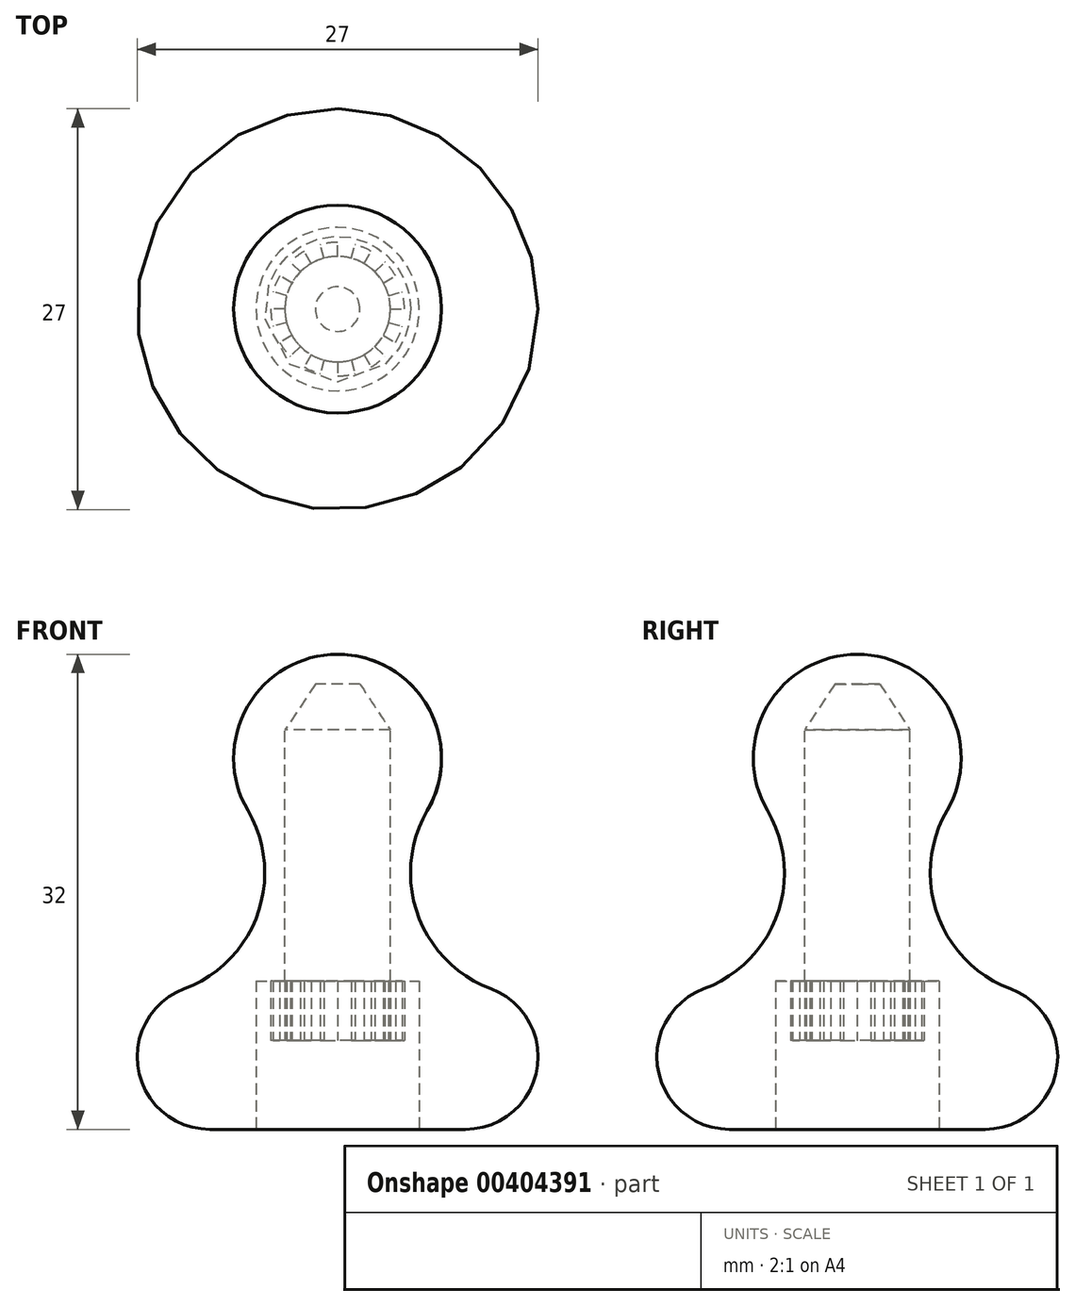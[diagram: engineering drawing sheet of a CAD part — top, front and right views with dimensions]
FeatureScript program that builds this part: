
annotation { "Feature Type Name" : "Feature", "Feature Type Description" : "" }
export const myFeature = defineFeature(function(context is Context, id is Id, definition is map)
    precondition{}
    {
        {
            var Q0;
            Q0=qCreatedBy(makeId("Top.planeOp"),FACE);
            var sketch = newSketch(context, id + "F0", { "sketchPlane" : qUnion([Q0])});
            skCircle(sketch, "E0", {"center": v(0, 0) * mm, "radius": 1.5 * mm});
            skCircle(sketch, "E1", {"center": v(0, 0) * mm, "radius": 3.55 * mm});
            skSolve(sketch);
        }
        {
            var Q0;
            Q0=makeQuery(id+"F0.imprint","IMPRINT",FACE,{"disambiguationData":[TD([[makeQuery(id+"F0.imprint","IMPRINT",EDGE,{"derivedFrom":sQuery(id+"F0.wireOp",EDGE,"BnrdN14r-d7P1-VGVA-sCLp-GcmtuHxksNj9")}),-1.0]])]});
            var Q1;
            Q1=makeQuery(id+"F0.imprint","IMPRINT",FACE,{"disambiguationData":[TD([[makeQuery(id+"F0.imprint","IMPRINT",EDGE,{"derivedFrom":sQuery(id+"F0.wireOp",EDGE,"E0")}),-1.0]])]});
            var Q2;
            Q2=makeQuery(id+"F0.imprint","IMPRINT",FACE,{"disambiguationData":[TD([[makeQuery(id+"F0.imprint","IMPRINT",EDGE,{"derivedFrom":sQuery(id+"F0.wireOp",EDGE,"E0")}),1.0]])]});
            extrude(context, id + "F1", {"entities" : qUnion([Q0, Q1, Q2]), "oppositeDirection" : true, "depth" : 50 * mm});
        }
        {
            var Q0;
            Q0=makeQuery(id+"F1.opExtrude","SWEPT_BODY",BODY,{"disambiguationData":[OSD([sQuery(id+"F0.wireOp",EDGE,"E1")])]});
            var Q1;
            Q1=qCreatedBy(makeId("Origin.pointOp"),VERTEX);
            transform(context, id + "F2", {"entities" : qUnion([Q0]), "transformType" : TransformType.TRANSLATION_3D, "dx" : 0 * mm, "dy" : 0 * mm, "dz" : -3.1 * mm, "makeCopy" : false});
        }
        {
            var Q1;
            Q1=makeQuery(id+"F1.opExtrude","CAP_FACE",FACE,{"disambiguationData":[OSD([sQuery(id+"F0.wireOp",EDGE,"E1")])],"isStart":true});
            var Q2;
            Q2=makeQuery(id+"F0.imprint","IMPRINT",FACE,{"disambiguationData":[TD([[makeQuery(id+"F0.imprint","IMPRINT",EDGE,{"derivedFrom":sQuery(id+"F0.wireOp",EDGE,"E0")}),1.0]])]});
            loft(context, id + "F3", {"operationType" : NewBodyOperationType.ADD, "sheetProfilesArray" : [{ "sheetProfileEntities" : qUnion([Q1]) }, { "sheetProfileEntities" : qUnion([Q2]) }]});
        }
        {
            var Q0;
            Q0=qCreatedBy(makeId("Front.planeOp"),FACE);
            var sketch = newSketch(context, id + "F4", { "sketchPlane" : qUnion([Q0])});
            skLineSegment(sketch, "E2", {"start": v(0, -30) * mm, "end": v(-8.6, -30) * mm});
            skArc(sketch, "E3", {"start": v(-8.6, -30) * mm, "mid": v(-13.42, -25.98) * mm, "end": v(-10.32, -20.53) * mm});
            skArc(sketch, "E4", {"start": v(-10.32, -20.53) * mm, "mid": v(-5.4, -15.52) * mm, "end": v(-6.05, -8.53) * mm});
            skArc(sketch, "E5", {"start": v(-6.05, -8.53) * mm, "mid": v(-6.07, -1.51) * mm, "end": v(0, 2) * mm});
            skLineSegment(sketch, "E6", {"start": v(-13.5, -15.08) * mm, "end": v(-13.5, -31) * mm, "construction": true});
            skLineSegment(sketch, "E7", {"start": v(0, 2) * mm, "end": v(0, -30) * mm});
            skSolve(sketch);
        }
        {
            var Q0;
            Q0=makeQuery(id+"F4.imprint","IMPRINT",FACE,{"disambiguationData":[TD([[makeQuery(id+"F4.imprint","IMPRINT",EDGE,{"derivedFrom":sQuery(id+"F4.wireOp",EDGE,"E2")}),-1.0]])]});
            var Q1;
            Q1=sQuery(id+"F4.wireOp",EDGE,"E7");
            revolve(context, id + "F5", {"entities" : qUnion([Q0]), "axis" : qUnion([Q1]), "revolveType" : RevolveType.FULL});
        }
        {
            var Q0;
            Q0=makeQuery(id+"F5.opRevolve","SWEPT_FACE",FACE,{"disambiguationData":[OSD([sQuery(id+"F4.wireOp",EDGE,"E2")])]});
            var sketch = newSketch(context, id + "F6", { "sketchPlane" : qUnion([Q0])});
            skCircle(sketch, "E8", {"center": v(0, 0) * mm, "radius": 3.15 * mm});
            skCircle(sketch, "E9", {"center": v(0, 0) * mm, "radius": 3.55 * mm});
            skCircle(sketch, "E10", {"center": v(0, 0) * mm, "radius": 5.5 * mm});
            skCircle(sketch, "E11", {"center": v(0, 0) * mm, "radius": 4.5 * mm});
            skLineSegment(sketch, "E12", {"start": v(-3.15, 0) * mm, "end": v(-4.5, 0) * mm});
            skLineSegment(sketch, "E13.1.0", {"start": v(-3.04, -0.82) * mm, "end": v(-4.35, -1.16) * mm});
            skLineSegment(sketch, "E13.2.0", {"start": v(-2.73, -1.57) * mm, "end": v(-3.9, -2.25) * mm});
            skLineSegment(sketch, "E13.3.0", {"start": v(-2.23, -2.23) * mm, "end": v(-3.18, -3.18) * mm});
            skLineSegment(sketch, "E13.4.0", {"start": v(-1.58, -2.73) * mm, "end": v(-2.25, -3.9) * mm});
            skLineSegment(sketch, "E13.5.0", {"start": v(-0.82, -3.04) * mm, "end": v(-1.16, -4.35) * mm});
            skLineSegment(sketch, "E13.6.0", {"start": v(0, -3.15) * mm, "end": v(0, -4.5) * mm});
            skLineSegment(sketch, "E13.7.0", {"start": v(0.82, -3.04) * mm, "end": v(1.16, -4.35) * mm});
            skLineSegment(sketch, "E13.8.0", {"start": v(1.57, -2.73) * mm, "end": v(2.25, -3.9) * mm});
            skLineSegment(sketch, "E13.9.0", {"start": v(2.23, -2.23) * mm, "end": v(3.18, -3.18) * mm});
            skLineSegment(sketch, "E13.10.0", {"start": v(2.73, -1.57) * mm, "end": v(3.9, -2.25) * mm});
            skLineSegment(sketch, "E13.11.0", {"start": v(3.04, -0.82) * mm, "end": v(4.35, -1.16) * mm});
            skLineSegment(sketch, "E13.12.0", {"start": v(3.15, 0) * mm, "end": v(4.5, 0) * mm});
            skLineSegment(sketch, "E13.13.0", {"start": v(3.04, 0.82) * mm, "end": v(4.35, 1.16) * mm});
            skLineSegment(sketch, "E13.14.0", {"start": v(2.73, 1.57) * mm, "end": v(3.9, 2.25) * mm});
            skLineSegment(sketch, "E13.15.0", {"start": v(2.23, 2.23) * mm, "end": v(3.18, 3.18) * mm});
            skLineSegment(sketch, "E13.16.0", {"start": v(1.58, 2.73) * mm, "end": v(2.25, 3.9) * mm});
            skLineSegment(sketch, "E13.17.0", {"start": v(0.82, 3.04) * mm, "end": v(1.16, 4.35) * mm});
            skLineSegment(sketch, "E13.18.0", {"start": v(0, 3.15) * mm, "end": v(0, 4.5) * mm});
            skLineSegment(sketch, "E13.19.0", {"start": v(-0.82, 3.04) * mm, "end": v(-1.16, 4.35) * mm});
            skLineSegment(sketch, "E13.20.0", {"start": v(-1.58, 2.73) * mm, "end": v(-2.25, 3.9) * mm});
            skLineSegment(sketch, "E13.21.0", {"start": v(-2.23, 2.23) * mm, "end": v(-3.18, 3.18) * mm});
            skLineSegment(sketch, "E13.22.0", {"start": v(-2.73, 1.58) * mm, "end": v(-3.9, 2.25) * mm});
            skLineSegment(sketch, "E13.23.0", {"start": v(-3.04, 0.82) * mm, "end": v(-4.35, 1.16) * mm});
            skSolve(sketch);
        }
        {
            var Q0;
            {var subQ0=sQuery(id+"F6.wireOp",EDGE,"O8we6DDi-UtpW-Hrfc-oVpV-u9EfWOaF4lRM");Q0=makeQuery(id+"F6.imprint","IMPRINT",FACE,{"disambiguationData":[TD([[makeQuery(id+"F6.imprint","IMPRINT",EDGE,{"derivedFrom":subQ0}),-1.0]])]});}
            var Q1;
            {var subQ0=sQuery(id+"F6.wireOp",EDGE,"c6f75dfc-24e0-407c-96d4-099803fd03f5.21.0");Q1=makeQuery(id+"F6.imprint","IMPRINT",FACE,{"disambiguationData":[TD([[makeQuery(id+"F6.imprint","IMPRINT",EDGE,{"derivedFrom":subQ0}),1.0]])]});}
            var Q2;
            {var subQ0=sQuery(id+"F6.wireOp",EDGE,"c6f75dfc-24e0-407c-96d4-099803fd03f5.19.0");Q2=makeQuery(id+"F6.imprint","IMPRINT",FACE,{"disambiguationData":[TD([[makeQuery(id+"F6.imprint","IMPRINT",EDGE,{"derivedFrom":subQ0}),1.0]])]});}
            var Q3;
            {var subQ0=sQuery(id+"F6.wireOp",EDGE,"c6f75dfc-24e0-407c-96d4-099803fd03f5.17.0");Q3=makeQuery(id+"F6.imprint","IMPRINT",FACE,{"disambiguationData":[TD([[makeQuery(id+"F6.imprint","IMPRINT",EDGE,{"derivedFrom":subQ0}),1.0]])]});}
            var Q4;
            {var subQ0=sQuery(id+"F6.wireOp",EDGE,"c6f75dfc-24e0-407c-96d4-099803fd03f5.15.0");Q4=makeQuery(id+"F6.imprint","IMPRINT",FACE,{"disambiguationData":[TD([[makeQuery(id+"F6.imprint","IMPRINT",EDGE,{"derivedFrom":subQ0}),1.0]])]});}
            var Q5;
            {var subQ0=sQuery(id+"F6.wireOp",EDGE,"c6f75dfc-24e0-407c-96d4-099803fd03f5.13.0");Q5=makeQuery(id+"F6.imprint","IMPRINT",FACE,{"disambiguationData":[TD([[makeQuery(id+"F6.imprint","IMPRINT",EDGE,{"derivedFrom":subQ0}),1.0]])]});}
            var Q6;
            {var subQ0=sQuery(id+"F6.wireOp",EDGE,"c6f75dfc-24e0-407c-96d4-099803fd03f5.11.0");Q6=makeQuery(id+"F6.imprint","IMPRINT",FACE,{"disambiguationData":[TD([[makeQuery(id+"F6.imprint","IMPRINT",EDGE,{"derivedFrom":subQ0}),1.0]])]});}
            var Q7;
            {var subQ0=sQuery(id+"F6.wireOp",EDGE,"c6f75dfc-24e0-407c-96d4-099803fd03f5.9.0");Q7=makeQuery(id+"F6.imprint","IMPRINT",FACE,{"disambiguationData":[TD([[makeQuery(id+"F6.imprint","IMPRINT",EDGE,{"derivedFrom":subQ0}),1.0]])]});}
            var Q8;
            {var subQ0=sQuery(id+"F6.wireOp",EDGE,"c6f75dfc-24e0-407c-96d4-099803fd03f5.7.0");Q8=makeQuery(id+"F6.imprint","IMPRINT",FACE,{"disambiguationData":[TD([[makeQuery(id+"F6.imprint","IMPRINT",EDGE,{"derivedFrom":subQ0}),1.0]])]});}
            var Q9;
            {var subQ0=sQuery(id+"F6.wireOp",EDGE,"c6f75dfc-24e0-407c-96d4-099803fd03f5.5.0");Q9=makeQuery(id+"F6.imprint","IMPRINT",FACE,{"disambiguationData":[TD([[makeQuery(id+"F6.imprint","IMPRINT",EDGE,{"derivedFrom":subQ0}),1.0]])]});}
            var Q10;
            {var subQ0=sQuery(id+"F6.wireOp",EDGE,"c6f75dfc-24e0-407c-96d4-099803fd03f5.3.0");Q10=makeQuery(id+"F6.imprint","IMPRINT",FACE,{"disambiguationData":[TD([[makeQuery(id+"F6.imprint","IMPRINT",EDGE,{"derivedFrom":subQ0}),1.0]])]});}
            var Q11;
            {var subQ0=sQuery(id+"F6.wireOp",EDGE,"c6f75dfc-24e0-407c-96d4-099803fd03f5.1.0");Q11=makeQuery(id+"F6.imprint","IMPRINT",FACE,{"disambiguationData":[TD([[makeQuery(id+"F6.imprint","IMPRINT",EDGE,{"derivedFrom":subQ0}),1.0]])]});}
            var Q12;
            {var subQ0=sQuery(id+"F6.wireOp",EDGE,"E13.23.0");var subQ1=sQuery(id+"F6.wireOp",EDGE,"E9");var subQ2=makeQuery(id+"F6.imprint","INTERSECT",VERTEX,{"derivedFrom":[subQ1,subQ0]});Q12=makeQuery(id+"F6.imprint","IMPRINT",FACE,{"disambiguationData":[TD([[makeQuery(id+"F6.imprint","IMPRINT",EDGE,{"disambiguationData":[TD([[subQ2,-1.0]])],"derivedFrom":subQ1}),-1.0]])]});}
            var Q13;
            {var subQ0=sQuery(id+"F6.wireOp",EDGE,"E12");var subQ1=sQuery(id+"F6.wireOp",EDGE,"E8");var subQ2=makeQuery(id+"F6.imprint","INTERSECT",VERTEX,{"derivedFrom":[subQ1,subQ0]});Q13=makeQuery(id+"F6.imprint","IMPRINT",FACE,{"disambiguationData":[TD([[makeQuery(id+"F6.imprint","IMPRINT",EDGE,{"disambiguationData":[TD([[subQ2,1.0]])],"derivedFrom":subQ1}),-1.0]])]});}
            var Q14;
            {var subQ0=sQuery(id+"F6.wireOp",EDGE,"E13.21.0");var subQ1=sQuery(id+"F6.wireOp",EDGE,"E8");var subQ2=makeQuery(id+"F6.imprint","INTERSECT",VERTEX,{"derivedFrom":[subQ1,subQ0]});Q14=makeQuery(id+"F6.imprint","IMPRINT",FACE,{"disambiguationData":[TD([[makeQuery(id+"F6.imprint","IMPRINT",EDGE,{"disambiguationData":[TD([[subQ2,-1.0]])],"derivedFrom":subQ1}),-1.0]])]});}
            var Q15;
            {var subQ0=sQuery(id+"F6.wireOp",EDGE,"E13.21.0");var subQ1=sQuery(id+"F6.wireOp",EDGE,"E9");var subQ2=makeQuery(id+"F6.imprint","INTERSECT",VERTEX,{"derivedFrom":[subQ1,subQ0]});Q15=makeQuery(id+"F6.imprint","IMPRINT",FACE,{"disambiguationData":[TD([[makeQuery(id+"F6.imprint","IMPRINT",EDGE,{"disambiguationData":[TD([[subQ2,-1.0]])],"derivedFrom":subQ1}),-1.0]])]});}
            var Q16;
            {var subQ0=sQuery(id+"F6.wireOp",EDGE,"E13.19.0");var subQ1=sQuery(id+"F6.wireOp",EDGE,"E9");var subQ2=makeQuery(id+"F6.imprint","INTERSECT",VERTEX,{"derivedFrom":[subQ1,subQ0]});Q16=makeQuery(id+"F6.imprint","IMPRINT",FACE,{"disambiguationData":[TD([[makeQuery(id+"F6.imprint","IMPRINT",EDGE,{"disambiguationData":[TD([[subQ2,-1.0]])],"derivedFrom":subQ1}),-1.0]])]});}
            var Q17;
            {var subQ0=sQuery(id+"F6.wireOp",EDGE,"E13.19.0");var subQ1=sQuery(id+"F6.wireOp",EDGE,"E8");var subQ2=makeQuery(id+"F6.imprint","INTERSECT",VERTEX,{"derivedFrom":[subQ1,subQ0]});Q17=makeQuery(id+"F6.imprint","IMPRINT",FACE,{"disambiguationData":[TD([[makeQuery(id+"F6.imprint","IMPRINT",EDGE,{"disambiguationData":[TD([[subQ2,-1.0]])],"derivedFrom":subQ1}),-1.0]])]});}
            var Q18;
            {var subQ0=sQuery(id+"F6.wireOp",EDGE,"E13.17.0");var subQ1=sQuery(id+"F6.wireOp",EDGE,"E9");var subQ2=makeQuery(id+"F6.imprint","INTERSECT",VERTEX,{"derivedFrom":[subQ1,subQ0]});Q18=makeQuery(id+"F6.imprint","IMPRINT",FACE,{"disambiguationData":[TD([[makeQuery(id+"F6.imprint","IMPRINT",EDGE,{"disambiguationData":[TD([[subQ2,-1.0]])],"derivedFrom":subQ1}),-1.0]])]});}
            var Q19;
            {var subQ0=sQuery(id+"F6.wireOp",EDGE,"E13.17.0");var subQ1=sQuery(id+"F6.wireOp",EDGE,"E8");var subQ2=makeQuery(id+"F6.imprint","INTERSECT",VERTEX,{"derivedFrom":[subQ1,subQ0]});Q19=makeQuery(id+"F6.imprint","IMPRINT",FACE,{"disambiguationData":[TD([[makeQuery(id+"F6.imprint","IMPRINT",EDGE,{"disambiguationData":[TD([[subQ2,-1.0]])],"derivedFrom":subQ1}),-1.0]])]});}
            var Q20;
            {var subQ0=sQuery(id+"F6.wireOp",EDGE,"E13.15.0");var subQ1=sQuery(id+"F6.wireOp",EDGE,"E9");var subQ2=makeQuery(id+"F6.imprint","INTERSECT",VERTEX,{"derivedFrom":[subQ1,subQ0]});Q20=makeQuery(id+"F6.imprint","IMPRINT",FACE,{"disambiguationData":[TD([[makeQuery(id+"F6.imprint","IMPRINT",EDGE,{"disambiguationData":[TD([[subQ2,-1.0]])],"derivedFrom":subQ1}),-1.0]])]});}
            var Q21;
            {var subQ0=sQuery(id+"F6.wireOp",EDGE,"E13.15.0");var subQ1=sQuery(id+"F6.wireOp",EDGE,"E8");var subQ2=makeQuery(id+"F6.imprint","INTERSECT",VERTEX,{"derivedFrom":[subQ1,subQ0]});Q21=makeQuery(id+"F6.imprint","IMPRINT",FACE,{"disambiguationData":[TD([[makeQuery(id+"F6.imprint","IMPRINT",EDGE,{"disambiguationData":[TD([[subQ2,-1.0]])],"derivedFrom":subQ1}),-1.0]])]});}
            var Q22;
            {var subQ0=sQuery(id+"F6.wireOp",EDGE,"E13.13.0");var subQ1=sQuery(id+"F6.wireOp",EDGE,"E9");var subQ2=makeQuery(id+"F6.imprint","INTERSECT",VERTEX,{"derivedFrom":[subQ1,subQ0]});Q22=makeQuery(id+"F6.imprint","IMPRINT",FACE,{"disambiguationData":[TD([[makeQuery(id+"F6.imprint","IMPRINT",EDGE,{"disambiguationData":[TD([[subQ2,-1.0]])],"derivedFrom":subQ1}),-1.0]])]});}
            var Q23;
            {var subQ0=sQuery(id+"F6.wireOp",EDGE,"E13.13.0");var subQ1=sQuery(id+"F6.wireOp",EDGE,"E8");var subQ2=makeQuery(id+"F6.imprint","INTERSECT",VERTEX,{"derivedFrom":[subQ1,subQ0]});Q23=makeQuery(id+"F6.imprint","IMPRINT",FACE,{"disambiguationData":[TD([[makeQuery(id+"F6.imprint","IMPRINT",EDGE,{"disambiguationData":[TD([[subQ2,-1.0]])],"derivedFrom":subQ1}),-1.0]])]});}
            var Q24;
            {var subQ0=sQuery(id+"F6.wireOp",EDGE,"E13.11.0");var subQ1=sQuery(id+"F6.wireOp",EDGE,"E8");var subQ2=makeQuery(id+"F6.imprint","INTERSECT",VERTEX,{"derivedFrom":[subQ1,subQ0]});Q24=makeQuery(id+"F6.imprint","IMPRINT",FACE,{"disambiguationData":[TD([[makeQuery(id+"F6.imprint","IMPRINT",EDGE,{"disambiguationData":[TD([[subQ2,-1.0]])],"derivedFrom":subQ1}),-1.0]])]});}
            var Q25;
            {var subQ0=sQuery(id+"F6.wireOp",EDGE,"E13.12.0");var subQ1=sQuery(id+"F6.wireOp",EDGE,"E9");var subQ2=makeQuery(id+"F6.imprint","INTERSECT",VERTEX,{"derivedFrom":[subQ1,subQ0]});Q25=makeQuery(id+"F6.imprint","IMPRINT",FACE,{"disambiguationData":[TD([[makeQuery(id+"F6.imprint","IMPRINT",EDGE,{"disambiguationData":[TD([[subQ2,1.0]])],"derivedFrom":subQ1}),-1.0]])]});}
            var Q26;
            {var subQ0=sQuery(id+"F6.wireOp",EDGE,"E13.9.0");var subQ1=sQuery(id+"F6.wireOp",EDGE,"E9");var subQ2=makeQuery(id+"F6.imprint","INTERSECT",VERTEX,{"derivedFrom":[subQ1,subQ0]});Q26=makeQuery(id+"F6.imprint","IMPRINT",FACE,{"disambiguationData":[TD([[makeQuery(id+"F6.imprint","IMPRINT",EDGE,{"disambiguationData":[TD([[subQ2,-1.0]])],"derivedFrom":subQ1}),-1.0]])]});}
            var Q27;
            {var subQ0=sQuery(id+"F6.wireOp",EDGE,"E13.9.0");var subQ1=sQuery(id+"F6.wireOp",EDGE,"E8");var subQ2=makeQuery(id+"F6.imprint","INTERSECT",VERTEX,{"derivedFrom":[subQ1,subQ0]});Q27=makeQuery(id+"F6.imprint","IMPRINT",FACE,{"disambiguationData":[TD([[makeQuery(id+"F6.imprint","IMPRINT",EDGE,{"disambiguationData":[TD([[subQ2,-1.0]])],"derivedFrom":subQ1}),-1.0]])]});}
            var Q28;
            {var subQ0=sQuery(id+"F6.wireOp",EDGE,"E13.7.0");var subQ1=sQuery(id+"F6.wireOp",EDGE,"E9");var subQ2=makeQuery(id+"F6.imprint","INTERSECT",VERTEX,{"derivedFrom":[subQ1,subQ0]});Q28=makeQuery(id+"F6.imprint","IMPRINT",FACE,{"disambiguationData":[TD([[makeQuery(id+"F6.imprint","IMPRINT",EDGE,{"disambiguationData":[TD([[subQ2,-1.0]])],"derivedFrom":subQ1}),-1.0]])]});}
            var Q29;
            {var subQ0=sQuery(id+"F6.wireOp",EDGE,"E13.7.0");var subQ1=sQuery(id+"F6.wireOp",EDGE,"E8");var subQ2=makeQuery(id+"F6.imprint","INTERSECT",VERTEX,{"derivedFrom":[subQ1,subQ0]});Q29=makeQuery(id+"F6.imprint","IMPRINT",FACE,{"disambiguationData":[TD([[makeQuery(id+"F6.imprint","IMPRINT",EDGE,{"disambiguationData":[TD([[subQ2,-1.0]])],"derivedFrom":subQ1}),-1.0]])]});}
            var Q30;
            {var subQ0=sQuery(id+"F6.wireOp",EDGE,"E13.5.0");var subQ1=sQuery(id+"F6.wireOp",EDGE,"E9");var subQ2=makeQuery(id+"F6.imprint","INTERSECT",VERTEX,{"derivedFrom":[subQ1,subQ0]});Q30=makeQuery(id+"F6.imprint","IMPRINT",FACE,{"disambiguationData":[TD([[makeQuery(id+"F6.imprint","IMPRINT",EDGE,{"disambiguationData":[TD([[subQ2,-1.0]])],"derivedFrom":subQ1}),-1.0]])]});}
            var Q31;
            {var subQ0=sQuery(id+"F6.wireOp",EDGE,"E13.5.0");var subQ1=sQuery(id+"F6.wireOp",EDGE,"E8");var subQ2=makeQuery(id+"F6.imprint","INTERSECT",VERTEX,{"derivedFrom":[subQ1,subQ0]});Q31=makeQuery(id+"F6.imprint","IMPRINT",FACE,{"disambiguationData":[TD([[makeQuery(id+"F6.imprint","IMPRINT",EDGE,{"disambiguationData":[TD([[subQ2,-1.0]])],"derivedFrom":subQ1}),-1.0]])]});}
            var Q32;
            {var subQ0=sQuery(id+"F6.wireOp",EDGE,"E13.3.0");var subQ1=sQuery(id+"F6.wireOp",EDGE,"E8");var subQ2=makeQuery(id+"F6.imprint","INTERSECT",VERTEX,{"derivedFrom":[subQ1,subQ0]});Q32=makeQuery(id+"F6.imprint","IMPRINT",FACE,{"disambiguationData":[TD([[makeQuery(id+"F6.imprint","IMPRINT",EDGE,{"disambiguationData":[TD([[subQ2,-1.0]])],"derivedFrom":subQ1}),-1.0]])]});}
            var Q33;
            {var subQ0=sQuery(id+"F6.wireOp",EDGE,"E13.3.0");var subQ1=sQuery(id+"F6.wireOp",EDGE,"E9");var subQ2=makeQuery(id+"F6.imprint","INTERSECT",VERTEX,{"derivedFrom":[subQ1,subQ0]});Q33=makeQuery(id+"F6.imprint","IMPRINT",FACE,{"disambiguationData":[TD([[makeQuery(id+"F6.imprint","IMPRINT",EDGE,{"disambiguationData":[TD([[subQ2,-1.0]])],"derivedFrom":subQ1}),-1.0]])]});}
            var Q34;
            {var subQ0=sQuery(id+"F6.wireOp",EDGE,"E13.1.0");var subQ1=sQuery(id+"F6.wireOp",EDGE,"E8");var subQ2=makeQuery(id+"F6.imprint","INTERSECT",VERTEX,{"derivedFrom":[subQ1,subQ0]});Q34=makeQuery(id+"F6.imprint","IMPRINT",FACE,{"disambiguationData":[TD([[makeQuery(id+"F6.imprint","IMPRINT",EDGE,{"disambiguationData":[TD([[subQ2,-1.0]])],"derivedFrom":subQ1}),-1.0]])]});}
            var Q35;
            {var subQ0=sQuery(id+"F6.wireOp",EDGE,"E13.1.0");var subQ1=sQuery(id+"F6.wireOp",EDGE,"E9");var subQ2=makeQuery(id+"F6.imprint","INTERSECT",VERTEX,{"derivedFrom":[subQ1,subQ0]});Q35=makeQuery(id+"F6.imprint","IMPRINT",FACE,{"disambiguationData":[TD([[makeQuery(id+"F6.imprint","IMPRINT",EDGE,{"disambiguationData":[TD([[subQ2,-1.0]])],"derivedFrom":subQ1}),-1.0]])]});}
            extrude(context, id + "F7", {"entities" : qUnion([Q0, Q1, Q2, Q3, Q4, Q5, Q6, Q7, Q8, Q9, Q10, Q11, Q12, Q13, Q14, Q15, Q16, Q17, Q18, Q19, Q20, Q21, Q22, Q23, Q24, Q25, Q26, Q27, Q28, Q29, Q30, Q31, Q32, Q33, Q34, Q35]), "operationType" : NewBodyOperationType.REMOVE, "oppositeDirection" : true, "depth" : 6 * mm});
        }
        {
            var Q0;
            Q0=makeQuery(id+"F1.opExtrude","SWEPT_BODY",BODY,{"disambiguationData":[OSD([sQuery(id+"F0.wireOp",EDGE,"E1")])]});
            var Q1;
            Q1=makeQuery(id+"F5.opRevolve","SWEPT_BODY",BODY,{"disambiguationData":[OSD([sQuery(id+"F4.wireOp",EDGE,"0b3e5e39-d095-4197-80f5-2699158d9401"),sQuery(id+"F4.wireOp",EDGE,"17098c68-7adf-4d78-b214-12c12919cdef"),sQuery(id+"F4.wireOp",EDGE,"E2"),sQuery(id+"F4.wireOp",EDGE,"E3"),sQuery(id+"F4.wireOp",EDGE,"E4"),sQuery(id+"F4.wireOp",EDGE,"E5"),sQuery(id+"F4.wireOp",EDGE,"hfa3zwkB-BSRJ-9cnI-bxZf-GsWjs4TLEIAJ")])]});
            booleanBodies(context, id + "F8", {"operationType" : BooleanOperationType.SUBTRACTION, "tools" : qUnion([Q0]), "targets" : qUnion([Q1])});
        }
        {
            var Q0;
            Q0=makeQuery(id+"F6.imprint","IMPRINT",FACE,{"disambiguationData":[TD([[makeQuery(id+"F6.imprint","IMPRINT",EDGE,{"derivedFrom":sQuery(id+"F6.wireOp",EDGE,"E10")}),1.0]])]});
            extrude(context, id + "F9", {"entities" : qUnion([Q0]), "operationType" : NewBodyOperationType.REMOVE, "oppositeDirection" : true, "depth" : 10 * mm});
        }
        {
            var Q0;
            {var subQ0=sQuery(id+"F6.wireOp",EDGE,"c6f75dfc-24e0-407c-96d4-099803fd03f5.20.0");Q0=makeQuery(id+"F6.imprint","IMPRINT",FACE,{"disambiguationData":[TD([[makeQuery(id+"F6.imprint","IMPRINT",EDGE,{"derivedFrom":subQ0}),1.0]])]});}
            var Q1;
            {var subQ0=sQuery(id+"F6.wireOp",EDGE,"c6f75dfc-24e0-407c-96d4-099803fd03f5.16.0");Q1=makeQuery(id+"F6.imprint","IMPRINT",FACE,{"disambiguationData":[TD([[makeQuery(id+"F6.imprint","IMPRINT",EDGE,{"derivedFrom":subQ0}),1.0]])]});}
            var Q2;
            {var subQ0=sQuery(id+"F6.wireOp",EDGE,"O8we6DDi-UtpW-Hrfc-oVpV-u9EfWOaF4lRM");Q2=makeQuery(id+"F6.imprint","IMPRINT",FACE,{"disambiguationData":[TD([[makeQuery(id+"F6.imprint","IMPRINT",EDGE,{"derivedFrom":subQ0}),-1.0]])]});}
            var Q3;
            {var subQ0=sQuery(id+"F6.wireOp",EDGE,"c6f75dfc-24e0-407c-96d4-099803fd03f5.4.0");Q3=makeQuery(id+"F6.imprint","IMPRINT",FACE,{"disambiguationData":[TD([[makeQuery(id+"F6.imprint","IMPRINT",EDGE,{"derivedFrom":subQ0}),1.0]])]});}
            var Q4;
            {var subQ0=sQuery(id+"F6.wireOp",EDGE,"c6f75dfc-24e0-407c-96d4-099803fd03f5.6.0");Q4=makeQuery(id+"F6.imprint","IMPRINT",FACE,{"disambiguationData":[TD([[makeQuery(id+"F6.imprint","IMPRINT",EDGE,{"derivedFrom":subQ0}),1.0]])]});}
            var Q5;
            {var subQ0=sQuery(id+"F6.wireOp",EDGE,"c6f75dfc-24e0-407c-96d4-099803fd03f5.7.0");Q5=makeQuery(id+"F6.imprint","IMPRINT",FACE,{"disambiguationData":[TD([[makeQuery(id+"F6.imprint","IMPRINT",EDGE,{"derivedFrom":subQ0}),1.0]])]});}
            var Q6;
            {var subQ0=sQuery(id+"F6.wireOp",EDGE,"c6f75dfc-24e0-407c-96d4-099803fd03f5.5.0");Q6=makeQuery(id+"F6.imprint","IMPRINT",FACE,{"disambiguationData":[TD([[makeQuery(id+"F6.imprint","IMPRINT",EDGE,{"derivedFrom":subQ0}),1.0]])]});}
            var Q7;
            {var subQ0=sQuery(id+"F6.wireOp",EDGE,"c6f75dfc-24e0-407c-96d4-099803fd03f5.19.0");Q7=makeQuery(id+"F6.imprint","IMPRINT",FACE,{"disambiguationData":[TD([[makeQuery(id+"F6.imprint","IMPRINT",EDGE,{"derivedFrom":subQ0}),1.0]])]});}
            var Q8;
            {var subQ0=sQuery(id+"F6.wireOp",EDGE,"c6f75dfc-24e0-407c-96d4-099803fd03f5.15.0");Q8=makeQuery(id+"F6.imprint","IMPRINT",FACE,{"disambiguationData":[TD([[makeQuery(id+"F6.imprint","IMPRINT",EDGE,{"derivedFrom":subQ0}),1.0]])]});}
            var Q9;
            {var subQ0=sQuery(id+"F6.wireOp",EDGE,"O8we6DDi-UtpW-Hrfc-oVpV-u9EfWOaF4lRM");Q9=makeQuery(id+"F6.imprint","IMPRINT",FACE,{"disambiguationData":[TD([[makeQuery(id+"F6.imprint","IMPRINT",EDGE,{"derivedFrom":subQ0}),1.0]])]});}
            var Q10;
            {var subQ0=sQuery(id+"F6.wireOp",EDGE,"c6f75dfc-24e0-407c-96d4-099803fd03f5.13.0");Q10=makeQuery(id+"F6.imprint","IMPRINT",FACE,{"disambiguationData":[TD([[makeQuery(id+"F6.imprint","IMPRINT",EDGE,{"derivedFrom":subQ0}),1.0]])]});}
            var Q11;
            {var subQ0=sQuery(id+"F6.wireOp",EDGE,"c6f75dfc-24e0-407c-96d4-099803fd03f5.12.0");Q11=makeQuery(id+"F6.imprint","IMPRINT",FACE,{"disambiguationData":[TD([[makeQuery(id+"F6.imprint","IMPRINT",EDGE,{"derivedFrom":subQ0}),1.0]])]});}
            var Q12;
            {var subQ0=sQuery(id+"F6.wireOp",EDGE,"c6f75dfc-24e0-407c-96d4-099803fd03f5.14.0");Q12=makeQuery(id+"F6.imprint","IMPRINT",FACE,{"disambiguationData":[TD([[makeQuery(id+"F6.imprint","IMPRINT",EDGE,{"derivedFrom":subQ0}),1.0]])]});}
            var Q13;
            {var subQ0=sQuery(id+"F6.wireOp",EDGE,"c6f75dfc-24e0-407c-96d4-099803fd03f5.17.0");Q13=makeQuery(id+"F6.imprint","IMPRINT",FACE,{"disambiguationData":[TD([[makeQuery(id+"F6.imprint","IMPRINT",EDGE,{"derivedFrom":subQ0}),1.0]])]});}
            var Q14;
            {var subQ0=sQuery(id+"F6.wireOp",EDGE,"c6f75dfc-24e0-407c-96d4-099803fd03f5.18.0");Q14=makeQuery(id+"F6.imprint","IMPRINT",FACE,{"disambiguationData":[TD([[makeQuery(id+"F6.imprint","IMPRINT",EDGE,{"derivedFrom":subQ0}),1.0]])]});}
            var Q15;
            {var subQ0=sQuery(id+"F6.wireOp",EDGE,"c6f75dfc-24e0-407c-96d4-099803fd03f5.21.0");Q15=makeQuery(id+"F6.imprint","IMPRINT",FACE,{"disambiguationData":[TD([[makeQuery(id+"F6.imprint","IMPRINT",EDGE,{"derivedFrom":subQ0}),1.0]])]});}
            var Q16;
            {var subQ0=sQuery(id+"F6.wireOp",EDGE,"c6f75dfc-24e0-407c-96d4-099803fd03f5.22.0");Q16=makeQuery(id+"F6.imprint","IMPRINT",FACE,{"disambiguationData":[TD([[makeQuery(id+"F6.imprint","IMPRINT",EDGE,{"derivedFrom":subQ0}),1.0]])]});}
            var Q17;
            {var subQ0=sQuery(id+"F6.wireOp",EDGE,"c6f75dfc-24e0-407c-96d4-099803fd03f5.1.0");Q17=makeQuery(id+"F6.imprint","IMPRINT",FACE,{"disambiguationData":[TD([[makeQuery(id+"F6.imprint","IMPRINT",EDGE,{"derivedFrom":subQ0}),1.0]])]});}
            var Q18;
            {var subQ0=sQuery(id+"F6.wireOp",EDGE,"c6f75dfc-24e0-407c-96d4-099803fd03f5.9.0");Q18=makeQuery(id+"F6.imprint","IMPRINT",FACE,{"disambiguationData":[TD([[makeQuery(id+"F6.imprint","IMPRINT",EDGE,{"derivedFrom":subQ0}),1.0]])]});}
            var Q19;
            {var subQ0=sQuery(id+"F6.wireOp",EDGE,"c6f75dfc-24e0-407c-96d4-099803fd03f5.3.0");Q19=makeQuery(id+"F6.imprint","IMPRINT",FACE,{"disambiguationData":[TD([[makeQuery(id+"F6.imprint","IMPRINT",EDGE,{"derivedFrom":subQ0}),1.0]])]});}
            var Q20;
            {var subQ0=sQuery(id+"F6.wireOp",EDGE,"c6f75dfc-24e0-407c-96d4-099803fd03f5.2.0");Q20=makeQuery(id+"F6.imprint","IMPRINT",FACE,{"disambiguationData":[TD([[makeQuery(id+"F6.imprint","IMPRINT",EDGE,{"derivedFrom":subQ0}),1.0]])]});}
            var Q21;
            {var subQ0=sQuery(id+"F6.wireOp",EDGE,"c6f75dfc-24e0-407c-96d4-099803fd03f5.11.0");Q21=makeQuery(id+"F6.imprint","IMPRINT",FACE,{"disambiguationData":[TD([[makeQuery(id+"F6.imprint","IMPRINT",EDGE,{"derivedFrom":subQ0}),1.0]])]});}
            var Q22;
            {var subQ0=sQuery(id+"F6.wireOp",EDGE,"c6f75dfc-24e0-407c-96d4-099803fd03f5.10.0");Q22=makeQuery(id+"F6.imprint","IMPRINT",FACE,{"disambiguationData":[TD([[makeQuery(id+"F6.imprint","IMPRINT",EDGE,{"derivedFrom":subQ0}),1.0]])]});}
            var Q23;
            {var subQ0=sQuery(id+"F6.wireOp",EDGE,"c6f75dfc-24e0-407c-96d4-099803fd03f5.8.0");Q23=makeQuery(id+"F6.imprint","IMPRINT",FACE,{"disambiguationData":[TD([[makeQuery(id+"F6.imprint","IMPRINT",EDGE,{"derivedFrom":subQ0}),1.0]])]});}
            var Q24;
            Q24=makeQuery(id+"F6.imprint","IMPRINT",FACE,{"disambiguationData":[TD([[makeQuery(id+"F6.imprint","IMPRINT",EDGE,{"derivedFrom":sQuery(id+"F6.wireOp",EDGE,"E11")}),1.0]])]});
            var Q25;
            {var subQ0=sQuery(id+"F6.wireOp",EDGE,"E13.1.0");var subQ1=sQuery(id+"F6.wireOp",EDGE,"E8");var subQ2=makeQuery(id+"F6.imprint","INTERSECT",VERTEX,{"derivedFrom":[subQ1,subQ0]});Q25=makeQuery(id+"F6.imprint","IMPRINT",FACE,{"disambiguationData":[TD([[makeQuery(id+"F6.imprint","IMPRINT",EDGE,{"disambiguationData":[TD([[subQ2,-1.0]])],"derivedFrom":subQ1}),-1.0]])]});}
            var Q26;
            {var subQ0=sQuery(id+"F6.wireOp",EDGE,"E12");var subQ1=sQuery(id+"F6.wireOp",EDGE,"E8");var subQ2=makeQuery(id+"F6.imprint","INTERSECT",VERTEX,{"derivedFrom":[subQ1,subQ0]});Q26=makeQuery(id+"F6.imprint","IMPRINT",FACE,{"disambiguationData":[TD([[makeQuery(id+"F6.imprint","IMPRINT",EDGE,{"disambiguationData":[TD([[subQ2,-1.0]])],"derivedFrom":subQ1}),-1.0]])]});}
            var Q27;
            {var subQ0=sQuery(id+"F6.wireOp",EDGE,"E12");var subQ1=sQuery(id+"F6.wireOp",EDGE,"E8");var subQ2=makeQuery(id+"F6.imprint","INTERSECT",VERTEX,{"derivedFrom":[subQ1,subQ0]});Q27=makeQuery(id+"F6.imprint","IMPRINT",FACE,{"disambiguationData":[TD([[makeQuery(id+"F6.imprint","IMPRINT",EDGE,{"disambiguationData":[TD([[subQ2,1.0]])],"derivedFrom":subQ1}),-1.0]])]});}
            var Q28;
            {var subQ0=sQuery(id+"F6.wireOp",EDGE,"E13.22.0");var subQ1=sQuery(id+"F6.wireOp",EDGE,"E8");var subQ2=makeQuery(id+"F6.imprint","INTERSECT",VERTEX,{"derivedFrom":[subQ1,subQ0]});Q28=makeQuery(id+"F6.imprint","IMPRINT",FACE,{"disambiguationData":[TD([[makeQuery(id+"F6.imprint","IMPRINT",EDGE,{"disambiguationData":[TD([[subQ2,-1.0]])],"derivedFrom":subQ1}),-1.0]])]});}
            var Q29;
            {var subQ0=sQuery(id+"F6.wireOp",EDGE,"E13.21.0");var subQ1=sQuery(id+"F6.wireOp",EDGE,"E8");var subQ2=makeQuery(id+"F6.imprint","INTERSECT",VERTEX,{"derivedFrom":[subQ1,subQ0]});Q29=makeQuery(id+"F6.imprint","IMPRINT",FACE,{"disambiguationData":[TD([[makeQuery(id+"F6.imprint","IMPRINT",EDGE,{"disambiguationData":[TD([[subQ2,-1.0]])],"derivedFrom":subQ1}),-1.0]])]});}
            var Q30;
            {var subQ0=sQuery(id+"F6.wireOp",EDGE,"E13.20.0");var subQ1=sQuery(id+"F6.wireOp",EDGE,"E8");var subQ2=makeQuery(id+"F6.imprint","INTERSECT",VERTEX,{"derivedFrom":[subQ1,subQ0]});Q30=makeQuery(id+"F6.imprint","IMPRINT",FACE,{"disambiguationData":[TD([[makeQuery(id+"F6.imprint","IMPRINT",EDGE,{"disambiguationData":[TD([[subQ2,-1.0]])],"derivedFrom":subQ1}),-1.0]])]});}
            var Q31;
            {var subQ0=sQuery(id+"F6.wireOp",EDGE,"E13.19.0");var subQ1=sQuery(id+"F6.wireOp",EDGE,"E8");var subQ2=makeQuery(id+"F6.imprint","INTERSECT",VERTEX,{"derivedFrom":[subQ1,subQ0]});Q31=makeQuery(id+"F6.imprint","IMPRINT",FACE,{"disambiguationData":[TD([[makeQuery(id+"F6.imprint","IMPRINT",EDGE,{"disambiguationData":[TD([[subQ2,-1.0]])],"derivedFrom":subQ1}),-1.0]])]});}
            var Q32;
            {var subQ0=sQuery(id+"F6.wireOp",EDGE,"E13.18.0");var subQ1=sQuery(id+"F6.wireOp",EDGE,"E8");var subQ2=makeQuery(id+"F6.imprint","INTERSECT",VERTEX,{"derivedFrom":[subQ1,subQ0]});Q32=makeQuery(id+"F6.imprint","IMPRINT",FACE,{"disambiguationData":[TD([[makeQuery(id+"F6.imprint","IMPRINT",EDGE,{"disambiguationData":[TD([[subQ2,-1.0]])],"derivedFrom":subQ1}),-1.0]])]});}
            var Q33;
            {var subQ0=sQuery(id+"F6.wireOp",EDGE,"E13.17.0");var subQ1=sQuery(id+"F6.wireOp",EDGE,"E8");var subQ2=makeQuery(id+"F6.imprint","INTERSECT",VERTEX,{"derivedFrom":[subQ1,subQ0]});Q33=makeQuery(id+"F6.imprint","IMPRINT",FACE,{"disambiguationData":[TD([[makeQuery(id+"F6.imprint","IMPRINT",EDGE,{"disambiguationData":[TD([[subQ2,-1.0]])],"derivedFrom":subQ1}),-1.0]])]});}
            var Q34;
            {var subQ0=sQuery(id+"F6.wireOp",EDGE,"E13.16.0");var subQ1=sQuery(id+"F6.wireOp",EDGE,"E8");var subQ2=makeQuery(id+"F6.imprint","INTERSECT",VERTEX,{"derivedFrom":[subQ1,subQ0]});Q34=makeQuery(id+"F6.imprint","IMPRINT",FACE,{"disambiguationData":[TD([[makeQuery(id+"F6.imprint","IMPRINT",EDGE,{"disambiguationData":[TD([[subQ2,-1.0]])],"derivedFrom":subQ1}),-1.0]])]});}
            var Q35;
            {var subQ0=sQuery(id+"F6.wireOp",EDGE,"E13.15.0");var subQ1=sQuery(id+"F6.wireOp",EDGE,"E8");var subQ2=makeQuery(id+"F6.imprint","INTERSECT",VERTEX,{"derivedFrom":[subQ1,subQ0]});Q35=makeQuery(id+"F6.imprint","IMPRINT",FACE,{"disambiguationData":[TD([[makeQuery(id+"F6.imprint","IMPRINT",EDGE,{"disambiguationData":[TD([[subQ2,-1.0]])],"derivedFrom":subQ1}),-1.0]])]});}
            var Q36;
            {var subQ0=sQuery(id+"F6.wireOp",EDGE,"E13.14.0");var subQ1=sQuery(id+"F6.wireOp",EDGE,"E8");var subQ2=makeQuery(id+"F6.imprint","INTERSECT",VERTEX,{"derivedFrom":[subQ1,subQ0]});Q36=makeQuery(id+"F6.imprint","IMPRINT",FACE,{"disambiguationData":[TD([[makeQuery(id+"F6.imprint","IMPRINT",EDGE,{"disambiguationData":[TD([[subQ2,-1.0]])],"derivedFrom":subQ1}),-1.0]])]});}
            var Q37;
            {var subQ0=sQuery(id+"F6.wireOp",EDGE,"E13.13.0");var subQ1=sQuery(id+"F6.wireOp",EDGE,"E8");var subQ2=makeQuery(id+"F6.imprint","INTERSECT",VERTEX,{"derivedFrom":[subQ1,subQ0]});Q37=makeQuery(id+"F6.imprint","IMPRINT",FACE,{"disambiguationData":[TD([[makeQuery(id+"F6.imprint","IMPRINT",EDGE,{"disambiguationData":[TD([[subQ2,-1.0]])],"derivedFrom":subQ1}),-1.0]])]});}
            var Q38;
            {var subQ0=sQuery(id+"F6.wireOp",EDGE,"E13.12.0");var subQ1=sQuery(id+"F6.wireOp",EDGE,"E8");var subQ2=makeQuery(id+"F6.imprint","INTERSECT",VERTEX,{"derivedFrom":[subQ1,subQ0]});Q38=makeQuery(id+"F6.imprint","IMPRINT",FACE,{"disambiguationData":[TD([[makeQuery(id+"F6.imprint","IMPRINT",EDGE,{"disambiguationData":[TD([[subQ2,-1.0]])],"derivedFrom":subQ1}),-1.0]])]});}
            var Q39;
            {var subQ0=sQuery(id+"F6.wireOp",EDGE,"E13.11.0");var subQ1=sQuery(id+"F6.wireOp",EDGE,"E8");var subQ2=makeQuery(id+"F6.imprint","INTERSECT",VERTEX,{"derivedFrom":[subQ1,subQ0]});Q39=makeQuery(id+"F6.imprint","IMPRINT",FACE,{"disambiguationData":[TD([[makeQuery(id+"F6.imprint","IMPRINT",EDGE,{"disambiguationData":[TD([[subQ2,-1.0]])],"derivedFrom":subQ1}),-1.0]])]});}
            var Q40;
            {var subQ0=sQuery(id+"F6.wireOp",EDGE,"E13.10.0");var subQ1=sQuery(id+"F6.wireOp",EDGE,"E8");var subQ2=makeQuery(id+"F6.imprint","INTERSECT",VERTEX,{"derivedFrom":[subQ1,subQ0]});Q40=makeQuery(id+"F6.imprint","IMPRINT",FACE,{"disambiguationData":[TD([[makeQuery(id+"F6.imprint","IMPRINT",EDGE,{"disambiguationData":[TD([[subQ2,-1.0]])],"derivedFrom":subQ1}),-1.0]])]});}
            var Q41;
            {var subQ0=sQuery(id+"F6.wireOp",EDGE,"E13.9.0");var subQ1=sQuery(id+"F6.wireOp",EDGE,"E8");var subQ2=makeQuery(id+"F6.imprint","INTERSECT",VERTEX,{"derivedFrom":[subQ1,subQ0]});Q41=makeQuery(id+"F6.imprint","IMPRINT",FACE,{"disambiguationData":[TD([[makeQuery(id+"F6.imprint","IMPRINT",EDGE,{"disambiguationData":[TD([[subQ2,-1.0]])],"derivedFrom":subQ1}),-1.0]])]});}
            var Q42;
            {var subQ0=sQuery(id+"F6.wireOp",EDGE,"E13.8.0");var subQ1=sQuery(id+"F6.wireOp",EDGE,"E8");var subQ2=makeQuery(id+"F6.imprint","INTERSECT",VERTEX,{"derivedFrom":[subQ1,subQ0]});Q42=makeQuery(id+"F6.imprint","IMPRINT",FACE,{"disambiguationData":[TD([[makeQuery(id+"F6.imprint","IMPRINT",EDGE,{"disambiguationData":[TD([[subQ2,-1.0]])],"derivedFrom":subQ1}),-1.0]])]});}
            var Q43;
            {var subQ0=sQuery(id+"F6.wireOp",EDGE,"E13.7.0");var subQ1=sQuery(id+"F6.wireOp",EDGE,"E8");var subQ2=makeQuery(id+"F6.imprint","INTERSECT",VERTEX,{"derivedFrom":[subQ1,subQ0]});Q43=makeQuery(id+"F6.imprint","IMPRINT",FACE,{"disambiguationData":[TD([[makeQuery(id+"F6.imprint","IMPRINT",EDGE,{"disambiguationData":[TD([[subQ2,-1.0]])],"derivedFrom":subQ1}),-1.0]])]});}
            var Q44;
            {var subQ0=sQuery(id+"F6.wireOp",EDGE,"E13.6.0");var subQ1=sQuery(id+"F6.wireOp",EDGE,"E8");var subQ2=makeQuery(id+"F6.imprint","INTERSECT",VERTEX,{"derivedFrom":[subQ1,subQ0]});Q44=makeQuery(id+"F6.imprint","IMPRINT",FACE,{"disambiguationData":[TD([[makeQuery(id+"F6.imprint","IMPRINT",EDGE,{"disambiguationData":[TD([[subQ2,-1.0]])],"derivedFrom":subQ1}),-1.0]])]});}
            var Q45;
            {var subQ0=sQuery(id+"F6.wireOp",EDGE,"E13.5.0");var subQ1=sQuery(id+"F6.wireOp",EDGE,"E8");var subQ2=makeQuery(id+"F6.imprint","INTERSECT",VERTEX,{"derivedFrom":[subQ1,subQ0]});Q45=makeQuery(id+"F6.imprint","IMPRINT",FACE,{"disambiguationData":[TD([[makeQuery(id+"F6.imprint","IMPRINT",EDGE,{"disambiguationData":[TD([[subQ2,-1.0]])],"derivedFrom":subQ1}),-1.0]])]});}
            var Q46;
            {var subQ0=sQuery(id+"F6.wireOp",EDGE,"E13.4.0");var subQ1=sQuery(id+"F6.wireOp",EDGE,"E8");var subQ2=makeQuery(id+"F6.imprint","INTERSECT",VERTEX,{"derivedFrom":[subQ1,subQ0]});Q46=makeQuery(id+"F6.imprint","IMPRINT",FACE,{"disambiguationData":[TD([[makeQuery(id+"F6.imprint","IMPRINT",EDGE,{"disambiguationData":[TD([[subQ2,-1.0]])],"derivedFrom":subQ1}),-1.0]])]});}
            var Q47;
            {var subQ0=sQuery(id+"F6.wireOp",EDGE,"E13.3.0");var subQ1=sQuery(id+"F6.wireOp",EDGE,"E8");var subQ2=makeQuery(id+"F6.imprint","INTERSECT",VERTEX,{"derivedFrom":[subQ1,subQ0]});Q47=makeQuery(id+"F6.imprint","IMPRINT",FACE,{"disambiguationData":[TD([[makeQuery(id+"F6.imprint","IMPRINT",EDGE,{"disambiguationData":[TD([[subQ2,-1.0]])],"derivedFrom":subQ1}),-1.0]])]});}
            var Q48;
            {var subQ0=sQuery(id+"F6.wireOp",EDGE,"E13.2.0");var subQ1=sQuery(id+"F6.wireOp",EDGE,"E8");var subQ2=makeQuery(id+"F6.imprint","INTERSECT",VERTEX,{"derivedFrom":[subQ1,subQ0]});Q48=makeQuery(id+"F6.imprint","IMPRINT",FACE,{"disambiguationData":[TD([[makeQuery(id+"F6.imprint","IMPRINT",EDGE,{"disambiguationData":[TD([[subQ2,-1.0]])],"derivedFrom":subQ1}),-1.0]])]});}
            extrude(context, id + "F10", {"entities" : qUnion([Q0, Q1, Q2, Q3, Q4, Q5, Q6, Q7, Q8, Q9, Q10, Q11, Q12, Q13, Q14, Q15, Q16, Q17, Q18, Q19, Q20, Q21, Q22, Q23, Q24, Q25, Q26, Q27, Q28, Q29, Q30, Q31, Q32, Q33, Q34, Q35, Q36, Q37, Q38, Q39, Q40, Q41, Q42, Q43, Q44, Q45, Q46, Q47, Q48]), "operationType" : NewBodyOperationType.REMOVE, "oppositeDirection" : true, "depth" : 5 * mm});
        }
        {
            var Q0;
            {var subQ0=sQuery(id+"F6.wireOp",EDGE,"E13.22.0");var subQ1=sQuery(id+"F6.wireOp",EDGE,"E9");var subQ2=makeQuery(id+"F6.imprint","INTERSECT",VERTEX,{"derivedFrom":[subQ1,subQ0]});Q0=makeQuery(id+"F6.imprint","IMPRINT",FACE,{"disambiguationData":[TD([[makeQuery(id+"F6.imprint","IMPRINT",EDGE,{"disambiguationData":[TD([[subQ2,-1.0]])],"derivedFrom":subQ1}),-1.0]])]});}
            var Q1;
            {var subQ0=sQuery(id+"F6.wireOp",EDGE,"E13.20.0");var subQ1=sQuery(id+"F6.wireOp",EDGE,"E9");var subQ2=makeQuery(id+"F6.imprint","INTERSECT",VERTEX,{"derivedFrom":[subQ1,subQ0]});Q1=makeQuery(id+"F6.imprint","IMPRINT",FACE,{"disambiguationData":[TD([[makeQuery(id+"F6.imprint","IMPRINT",EDGE,{"disambiguationData":[TD([[subQ2,-1.0]])],"derivedFrom":subQ1}),-1.0]])]});}
            var Q2;
            {var subQ0=sQuery(id+"F6.wireOp",EDGE,"E13.18.0");var subQ1=sQuery(id+"F6.wireOp",EDGE,"E9");var subQ2=makeQuery(id+"F6.imprint","INTERSECT",VERTEX,{"derivedFrom":[subQ1,subQ0]});Q2=makeQuery(id+"F6.imprint","IMPRINT",FACE,{"disambiguationData":[TD([[makeQuery(id+"F6.imprint","IMPRINT",EDGE,{"disambiguationData":[TD([[subQ2,-1.0]])],"derivedFrom":subQ1}),-1.0]])]});}
            var Q3;
            {var subQ0=sQuery(id+"F6.wireOp",EDGE,"E13.16.0");var subQ1=sQuery(id+"F6.wireOp",EDGE,"E9");var subQ2=makeQuery(id+"F6.imprint","INTERSECT",VERTEX,{"derivedFrom":[subQ1,subQ0]});Q3=makeQuery(id+"F6.imprint","IMPRINT",FACE,{"disambiguationData":[TD([[makeQuery(id+"F6.imprint","IMPRINT",EDGE,{"disambiguationData":[TD([[subQ2,-1.0]])],"derivedFrom":subQ1}),-1.0]])]});}
            var Q4;
            {var subQ0=sQuery(id+"F6.wireOp",EDGE,"E13.14.0");var subQ1=sQuery(id+"F6.wireOp",EDGE,"E9");var subQ2=makeQuery(id+"F6.imprint","INTERSECT",VERTEX,{"derivedFrom":[subQ1,subQ0]});Q4=makeQuery(id+"F6.imprint","IMPRINT",FACE,{"disambiguationData":[TD([[makeQuery(id+"F6.imprint","IMPRINT",EDGE,{"disambiguationData":[TD([[subQ2,-1.0]])],"derivedFrom":subQ1}),-1.0]])]});}
            var Q5;
            {var subQ0=sQuery(id+"F6.wireOp",EDGE,"E13.13.0");var subQ1=sQuery(id+"F6.wireOp",EDGE,"E9");var subQ2=makeQuery(id+"F6.imprint","INTERSECT",VERTEX,{"derivedFrom":[subQ1,subQ0]});Q5=makeQuery(id+"F6.imprint","IMPRINT",FACE,{"disambiguationData":[TD([[makeQuery(id+"F6.imprint","IMPRINT",EDGE,{"disambiguationData":[TD([[subQ2,1.0]])],"derivedFrom":subQ1}),-1.0]])]});}
            var Q6;
            {var subQ0=sQuery(id+"F6.wireOp",EDGE,"E13.10.0");var subQ1=sQuery(id+"F6.wireOp",EDGE,"E9");var subQ2=makeQuery(id+"F6.imprint","INTERSECT",VERTEX,{"derivedFrom":[subQ1,subQ0]});Q6=makeQuery(id+"F6.imprint","IMPRINT",FACE,{"disambiguationData":[TD([[makeQuery(id+"F6.imprint","IMPRINT",EDGE,{"disambiguationData":[TD([[subQ2,-1.0]])],"derivedFrom":subQ1}),-1.0]])]});}
            var Q7;
            {var subQ0=sQuery(id+"F6.wireOp",EDGE,"E13.8.0");var subQ1=sQuery(id+"F6.wireOp",EDGE,"E9");var subQ2=makeQuery(id+"F6.imprint","INTERSECT",VERTEX,{"derivedFrom":[subQ1,subQ0]});Q7=makeQuery(id+"F6.imprint","IMPRINT",FACE,{"disambiguationData":[TD([[makeQuery(id+"F6.imprint","IMPRINT",EDGE,{"disambiguationData":[TD([[subQ2,-1.0]])],"derivedFrom":subQ1}),-1.0]])]});}
            var Q8;
            {var subQ0=sQuery(id+"F6.wireOp",EDGE,"E13.6.0");var subQ1=sQuery(id+"F6.wireOp",EDGE,"E9");var subQ2=makeQuery(id+"F6.imprint","INTERSECT",VERTEX,{"derivedFrom":[subQ1,subQ0]});Q8=makeQuery(id+"F6.imprint","IMPRINT",FACE,{"disambiguationData":[TD([[makeQuery(id+"F6.imprint","IMPRINT",EDGE,{"disambiguationData":[TD([[subQ2,-1.0]])],"derivedFrom":subQ1}),-1.0]])]});}
            var Q9;
            {var subQ0=sQuery(id+"F6.wireOp",EDGE,"E13.4.0");var subQ1=sQuery(id+"F6.wireOp",EDGE,"E9");var subQ2=makeQuery(id+"F6.imprint","INTERSECT",VERTEX,{"derivedFrom":[subQ1,subQ0]});Q9=makeQuery(id+"F6.imprint","IMPRINT",FACE,{"disambiguationData":[TD([[makeQuery(id+"F6.imprint","IMPRINT",EDGE,{"disambiguationData":[TD([[subQ2,-1.0]])],"derivedFrom":subQ1}),-1.0]])]});}
            var Q10;
            {var subQ0=sQuery(id+"F6.wireOp",EDGE,"E13.2.0");var subQ1=sQuery(id+"F6.wireOp",EDGE,"E9");var subQ2=makeQuery(id+"F6.imprint","INTERSECT",VERTEX,{"derivedFrom":[subQ1,subQ0]});Q10=makeQuery(id+"F6.imprint","IMPRINT",FACE,{"disambiguationData":[TD([[makeQuery(id+"F6.imprint","IMPRINT",EDGE,{"disambiguationData":[TD([[subQ2,-1.0]])],"derivedFrom":subQ1}),-1.0]])]});}
            var Q11;
            {var subQ0=sQuery(id+"F6.wireOp",EDGE,"E12");var subQ1=sQuery(id+"F6.wireOp",EDGE,"E9");var subQ2=makeQuery(id+"F6.imprint","INTERSECT",VERTEX,{"derivedFrom":[subQ1,subQ0]});Q11=makeQuery(id+"F6.imprint","IMPRINT",FACE,{"disambiguationData":[TD([[makeQuery(id+"F6.imprint","IMPRINT",EDGE,{"disambiguationData":[TD([[subQ2,-1.0]])],"derivedFrom":subQ1}),-1.0]])]});}
            extrude(context, id + "F11", {"entities" : qUnion([Q0, Q1, Q2, Q3, Q4, Q5, Q6, Q7, Q8, Q9, Q10, Q11]), "operationType" : NewBodyOperationType.REMOVE, "oppositeDirection" : true, "depth" : 10 * mm});
        }
    });
